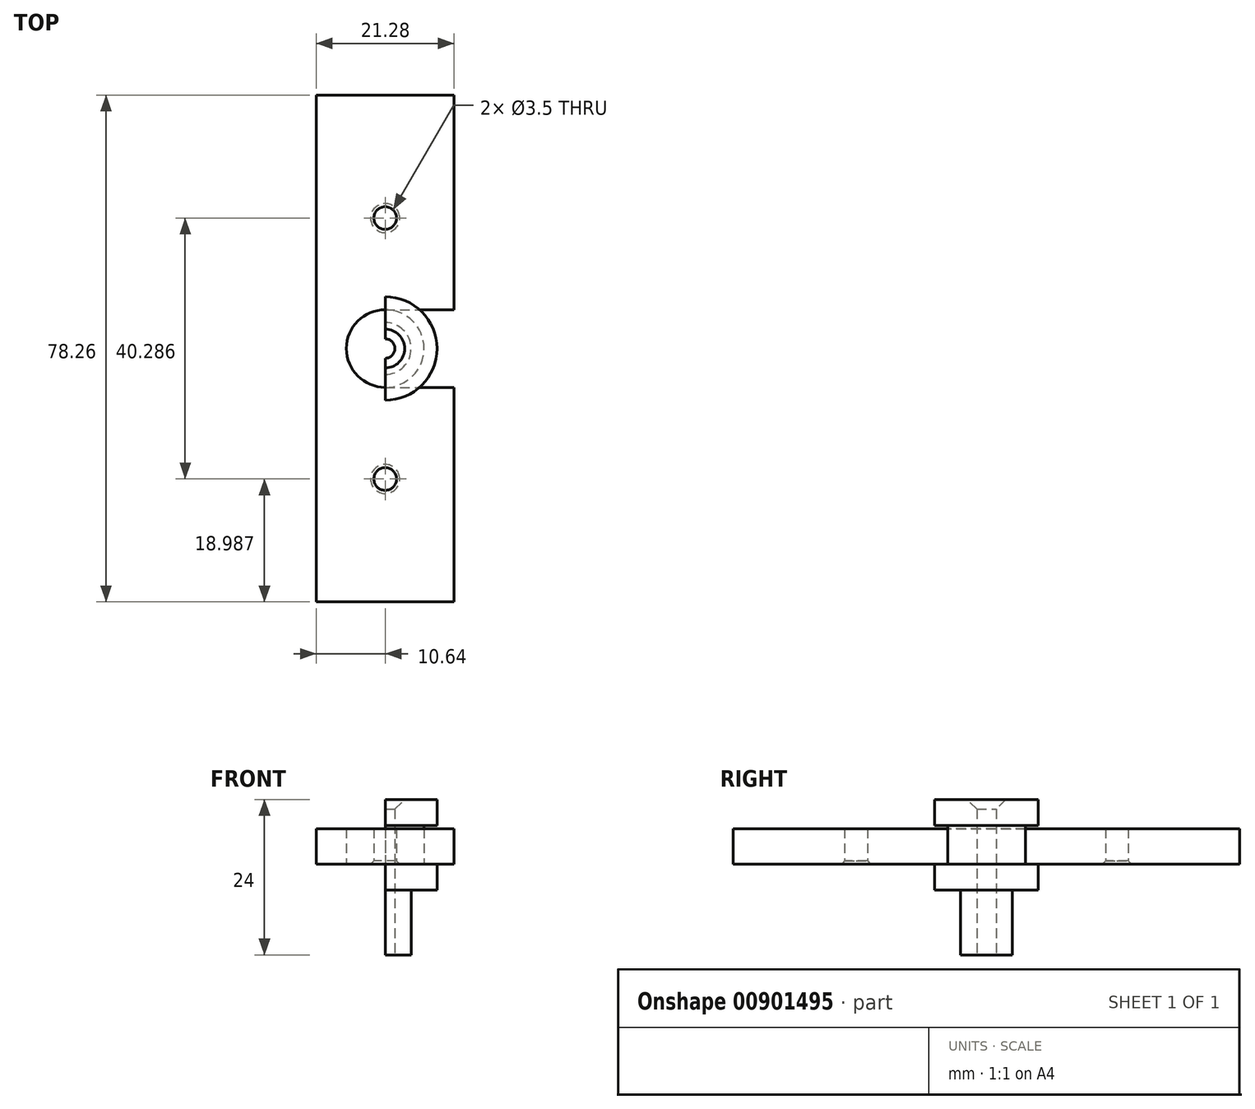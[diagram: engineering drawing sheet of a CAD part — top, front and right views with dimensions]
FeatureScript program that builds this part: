
annotation { "Feature Type Name" : "Feature", "Feature Type Description" : "" }
export const myFeature = defineFeature(function(context is Context, id is Id, definition is map)
    precondition{}
    {
        {
            var Q0;
            Q0=qCreatedBy(makeId("Top.planeOp"),FACE);
            var sketch = newSketch(context, id + "F0", { "sketchPlane" : qUnion([Q0])});
            skCircle(sketch, "E0", {"center": v(0, 0) * mm, "radius": 4 * mm});
            skCircle(sketch, "E1", {"center": v(0, 0) * mm, "radius": 1.5 * mm});
            skSolve(sketch);
        }
        {
            var Q0;
            Q0=makeQuery(id+"F0.imprint","IMPRINT",FACE,{"disambiguationData":[TD([[makeQuery(id+"F0.imprint","IMPRINT",EDGE,{"derivedFrom":sQuery(id+"F0.wireOp",EDGE,"E0")}),1.0]])]});
            var Q1;
            Q1=makeQuery(id+"F0.imprint","IMPRINT",FACE,{"disambiguationData":[TD([[makeQuery(id+"F0.imprint","IMPRINT",EDGE,{"derivedFrom":sQuery(id+"F0.wireOp",EDGE,"E1")}),1.0]])]});
            extrude(context, id + "F1", {"entities" : qUnion([Q0, Q1]), "depth" : 10 * mm, "offsetDistance" : 25 * mm});
        }
        {
            var Q0;
            Q0=makeQuery(id+"F1.opExtrude","CAP_FACE",FACE,{"disambiguationData":[OSD([sQuery(id+"F0.wireOp",EDGE,"E0"),sQuery(id+"F0.wireOp",EDGE,"E1")])],"isStart":false});
            var sketch = newSketch(context, id + "F2", { "sketchPlane" : qUnion([Q0])});
            skCircle(sketch, "E2", {"center": v(0, 0) * mm, "radius": 8 * mm});
            skSolve(sketch);
        }
        {
            var Q0;
            Q0 = qSketchRegion(id + "F2", true);
            extrude(context, id + "F3", {"entities" : qUnion([Q0]), "operationType" : NewBodyOperationType.ADD, "depth" : 4 * mm, "offsetDistance" : 25 * mm});
        }
        {
            var Q0;
            Q0=makeQuery(id+"F3.opExtrude","CAP_FACE",FACE,{"disambiguationData":[OSD([sQuery(id+"F2.wireOp",EDGE,"E2")])],"isStart":false});
            var sketch = newSketch(context, id + "F4", { "sketchPlane" : qUnion([Q0])});
            skCircle(sketch, "E3", {"center": v(0, 0) * mm, "radius": 6 * mm});
            skSolve(sketch);
        }
        {
            var Q0;
            Q0=makeQuery(id+"F4.imprint","IMPRINT",FACE,{"disambiguationData":[TD([[makeQuery(id+"F4.imprint","IMPRINT",EDGE,{"derivedFrom":sQuery(id+"F4.wireOp",EDGE,"E3")}),1.0]])]});
            extrude(context, id + "F5", {"entities" : qUnion([Q0]), "operationType" : NewBodyOperationType.ADD, "depth" : 6 * mm, "offsetDistance" : 25 * mm});
        }
        {
            var Q0;
            Q0=makeQuery(id+"F5.opExtrude","CAP_FACE",FACE,{"disambiguationData":[OSD([sQuery(id+"F4.wireOp",EDGE,"E3")])],"isStart":false});
            var sketch = newSketch(context, id + "F6", { "sketchPlane" : qUnion([Q0])});
            skCircle(sketch, "E4", {"center": v(0, 0) * mm, "radius": 8 * mm});
            skSolve(sketch);
        }
        {
            var Q0;
            Q0 = qSketchRegion(id + "F6", true);
            extrude(context, id + "F7", {"entities" : qUnion([Q0]), "operationType" : NewBodyOperationType.ADD, "depth" : 4 * mm, "offsetDistance" : 25 * mm});
        }
        {
            var Q0;
            Q0=makeQuery(id+"F0.imprint","IMPRINT",FACE,{"disambiguationData":[TD([[makeQuery(id+"F0.imprint","IMPRINT",EDGE,{"derivedFrom":sQuery(id+"F0.wireOp",EDGE,"E1")}),1.0]])]});
            extrude(context, id + "F8", {"entities" : qUnion([Q0]), "operationType" : NewBodyOperationType.REMOVE, "endBound" : BoundingType.THROUGH_ALL, "depth" : 25 * mm, "offsetDistance" : 25 * mm});
        }
        {
            var Q0;
            Q0=makeQuery(id+"F8.boolean.opBoolean","INTERSECT",EDGE,{"derivedFrom":[makeQuery(id+"F7.opExtrude","CAP_FACE",FACE,{"disambiguationData":[OSD([sQuery(id+"F6.wireOp",EDGE,"E4")])],"isStart":false}),makeQuery(id+"F8.opExtrude","SWEPT_FACE",FACE,{"disambiguationData":[OSD([sQuery(id+"F0.wireOp",EDGE,"E1")])]})]});
            chamfer(context, id + "F9", {"entities" : qUnion([Q0]), "width" : 1.5 * mm, "tangentPropagation" : true});
        }
        {
            var Q0;
            Q0=makeQuery(id+"F3.opExtrude","CAP_FACE",FACE,{"disambiguationData":[OSD([sQuery(id+"F2.wireOp",EDGE,"E2")])],"isStart":false});
            var sketch = newSketch(context, id + "F10", { "sketchPlane" : qUnion([Q0])});
            skLineSegment(sketch, "E5.bottom", {"start": v(-10.64, -39.13) * mm, "end": v(10.64, -39.13) * mm});
            skLineSegment(sketch, "E5.top", {"start": v(-10.64, 39.13) * mm, "end": v(10.64, 39.13) * mm});
            skLineSegment(sketch, "E5.left", {"start": v(-10.64, -39.13) * mm, "end": v(-10.64, 39.13) * mm});
            skLineSegment(sketch, "E5.right", {"start": v(10.64, -39.13) * mm, "end": v(10.64, 39.13) * mm});
            skPoint(sketch, "E5.middle", {"position": v(0, 0) * mm});
            skCircle(sketch, "E6.0", {"center": v(0, 0) * mm, "radius": 6 * mm});
            skCircle(sketch, "E7.0", {"center": v(0, 0) * mm, "radius": 8 * mm});
            skLineSegment(sketch, "E8", {"start": v(0, 6) * mm, "end": v(10.64, 6) * mm});
            skLineSegment(sketch, "E9", {"start": v(0, -6) * mm, "end": v(10.64, -6) * mm});
            skLineSegment(sketch, "E10", {"start": v(0, 39.13) * mm, "end": v(0, -39.13) * mm, "construction": true});
            skCircle(sketch, "E11", {"center": v(0, 20.14) * mm, "radius": 1.75 * mm});
            skLineSegment(sketch, "E12", {"start": v(-10.64, 0) * mm, "end": v(10.64, 0) * mm, "construction": true});
            skCircle(sketch, "E13.MirrorC", {"center": v(0, -20.14) * mm, "radius": 1.75 * mm});
            skSolve(sketch);
        }
        {
            var Q0;
            {var subQ1=sQuery(id+"F10.wireOp",EDGE,"E5.bottom");Q0=makeQuery(id+"F10.imprint","IMPRINT",FACE,{"disambiguationData":[TD([[makeQuery(id+"F10.imprint","IMPRINT",EDGE,{"derivedFrom":subQ1}),1.0]])]});}
            var Q1;
            {var subQ0=sQuery(id+"F10.wireOp",EDGE,"E8");var subQ1=sQuery(id+"F10.wireOp",EDGE,"E6.0");var subQ2=makeQuery(id+"F10.imprint","INTERSECT",VERTEX,{"derivedFrom":[subQ1,subQ0]});Q1=makeQuery(id+"F10.imprint","IMPRINT",FACE,{"disambiguationData":[TD([[makeQuery(id+"F10.imprint","IMPRINT",EDGE,{"disambiguationData":[TD([[subQ2,-1.0]])],"derivedFrom":subQ1}),-1.0]])]});}
            extrude(context, id + "F11", {"entities" : qUnion([Q0, Q1]), "depth" : 5.5 * mm, "offsetDistance" : 25 * mm});
        }
        {
            var Q0;
            Q0=makeQuery(id+"F11.opExtrude","CAP_EDGE",EDGE,{"disambiguationData":[OSD([sQuery(id+"F10.wireOp",EDGE,"E11")])],"isStart":true});
            var Q1;
            Q1=makeQuery(id+"F11.opExtrude","CAP_EDGE",EDGE,{"disambiguationData":[OSD([sQuery(id+"F10.wireOp",EDGE,"E13.MirrorC")])],"isStart":true});
            chamfer(context, id + "F12", {"entities" : qUnion([Q0, Q1]), "width" : 0.5 * mm, "tangentPropagation" : true});
        }
        {
            var Q0;
            Q0=makeQuery(id+"F7.opExtrude","CAP_FACE",FACE,{"disambiguationData":[OSD([sQuery(id+"F6.wireOp",EDGE,"E4")])],"isStart":false});
            var sketch = newSketch(context, id + "F13", { "sketchPlane" : qUnion([Q0])});
            skLineSegment(sketch, "E14.bottom", {"start": v(0, 8) * mm, "end": v(-9.04, 8) * mm});
            skLineSegment(sketch, "E14.top", {"start": v(0, -9.21) * mm, "end": v(-9.04, -9.21) * mm});
            skLineSegment(sketch, "E14.left", {"start": v(0, 8) * mm, "end": v(0, -9.21) * mm});
            skLineSegment(sketch, "E14.right", {"start": v(-9.04, 8) * mm, "end": v(-9.04, -9.21) * mm});
            skSolve(sketch);
        }
        {
            var Q0;
            Q0 = qSketchRegion(id + "F13", true);
            var Q1;
            Q1=makeQuery(id+"F1.opExtrude","CAP_FACE",FACE,{"disambiguationData":[OSD([sQuery(id+"F0.wireOp",EDGE,"E0")])],"isStart":true});
            extrude(context, id + "F14", {"entities" : qUnion([Q0]), "endBound" : BoundingType.UP_TO_SURFACE, "oppositeDirection" : true, "depth" : 25 * mm, "endBoundEntityFace" : qUnion([Q1]), "offsetDistance" : 25 * mm});
        }
        {
            var Q0;
            Q0=makeQuery(id+"F14.opExtrude","SWEPT_BODY",BODY,{"disambiguationData":[OSD([sQuery(id+"F13.wireOp",EDGE,"E14.bottom"),sQuery(id+"F13.wireOp",EDGE,"E14.top"),sQuery(id+"F13.wireOp",EDGE,"E14.left"),sQuery(id+"F13.wireOp",EDGE,"E14.right")])]});
            var Q1;
            Q1=makeQuery(id+"F1.opExtrude","SWEPT_BODY",BODY,{"disambiguationData":[OSD([sQuery(id+"F0.wireOp",EDGE,"E0")])]});
            booleanBodies(context, id + "F15", {"operationType" : BooleanOperationType.SUBTRACTION, "tools" : qUnion([Q0]), "targets" : qUnion([Q1])});
        }
    });
